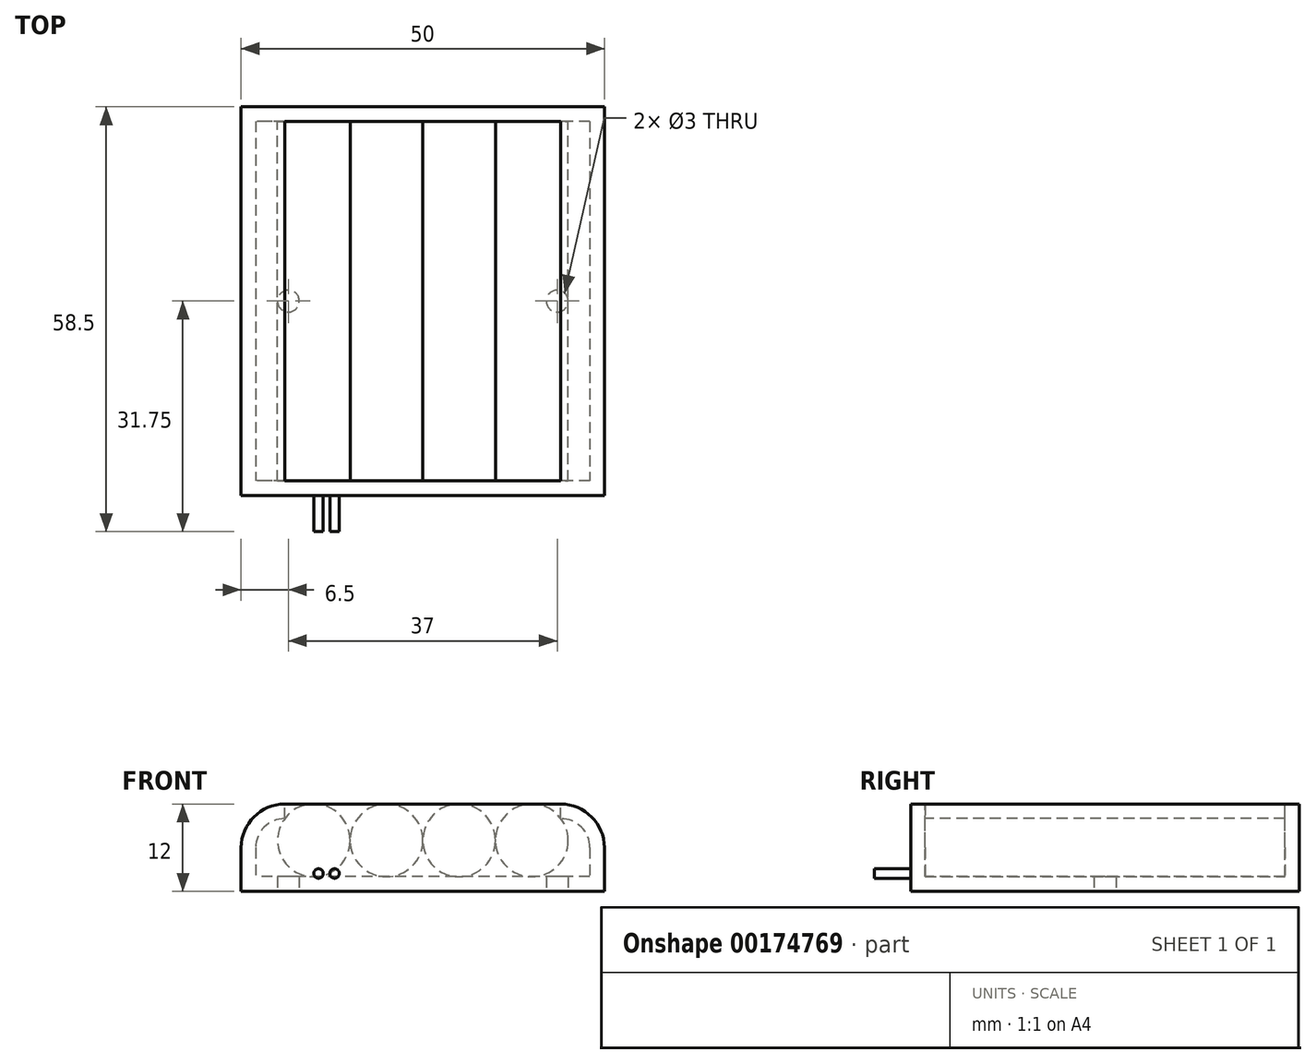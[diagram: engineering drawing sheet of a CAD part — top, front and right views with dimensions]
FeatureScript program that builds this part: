
annotation { "Feature Type Name" : "Feature", "Feature Type Description" : "" }
export const myFeature = defineFeature(function(context is Context, id is Id, definition is map)
    precondition{}
    {
        {
            var Q0;
            Q0=qCreatedBy(makeId("Top.planeOp"),FACE);
            var sketch = newSketch(context, id + "F0", { "sketchPlane" : qUnion([Q0])});
            skLineSegment(sketch, "E0.bottom", {"start": v(25, 26.75) * mm, "end": v(-25, 26.75) * mm});
            skLineSegment(sketch, "E0.top", {"start": v(25, -26.75) * mm, "end": v(-25, -26.75) * mm});
            skLineSegment(sketch, "E0.left", {"start": v(25, 26.75) * mm, "end": v(25, -26.75) * mm});
            skLineSegment(sketch, "E0.right", {"start": v(-25, 26.75) * mm, "end": v(-25, -26.75) * mm});
            skPoint(sketch, "E0.middle", {"position": v(0, 0) * mm});
            skSolve(sketch);
        }
        {
            var Q0;
            Q0=qSketchRegion(id+"F0",true);
            extrude(context, id + "F1", {"entities" : qUnion([Q0]), "depth" : 12 * mm, "offsetDistance" : 25 * mm});
        }
        {
            var Q0;
            Q0=makeQuery(id+"F1.opExtrude","CAP_EDGE",EDGE,{"disambiguationData":[OSD([sQuery(id+"F0.wireOp",EDGE,"E0.left")])],"isStart":false});
            var Q1;
            Q1=makeQuery(id+"F1.opExtrude","CAP_EDGE",EDGE,{"disambiguationData":[OSD([sQuery(id+"F0.wireOp",EDGE,"E0.right")])],"isStart":false});
            fillet(context, id + "F2", {"entities" : qUnion([Q0, Q1]), "radius" : 6 * mm, "tangentPropagation" : true, "allowEdgeOverflow" : false});
        }
        {
            var Q0;
            Q0=makeQuery(id+"F1.opExtrude","CAP_FACE",FACE,{"disambiguationData":[OSD([sQuery(id+"F0.wireOp",EDGE,"E0.bottom"),sQuery(id+"F0.wireOp",EDGE,"E0.top"),sQuery(id+"F0.wireOp",EDGE,"E0.left"),sQuery(id+"F0.wireOp",EDGE,"E0.right")])],"isStart":false});
            shell(context, id + "F3", {"entities" : qUnion([Q0]), "thickness" : 2 * mm});
        }
        {
            var Q0;
            Q0=makeQuery(id+"F1.opExtrude","CAP_FACE",FACE,{"disambiguationData":[OSD([sQuery(id+"F0.wireOp",EDGE,"E0.bottom"),sQuery(id+"F0.wireOp",EDGE,"E0.top"),sQuery(id+"F0.wireOp",EDGE,"E0.left"),sQuery(id+"F0.wireOp",EDGE,"E0.right")])],"isStart":true});
            var sketch = newSketch(context, id + "F4", { "sketchPlane" : qUnion([Q0])});
            skCircle(sketch, "E1", {"center": v(-18.5, 0) * mm, "radius": 1.5 * mm});
            skCircle(sketch, "E2.MirrorC", {"center": v(18.5, 0) * mm, "radius": 1.5 * mm});
            skSolve(sketch);
        }
        {
            var Q0;
            Q0=qSketchRegion(id+"F4",true);
            extrude(context, id + "F5", {"entities" : qUnion([Q0]), "operationType" : NewBodyOperationType.REMOVE, "oppositeDirection" : true, "depth" : 3 * mm, "offsetDistance" : 25 * mm});
        }
        {
            var Q0;
            Q0=makeQuery(id+"F1.opExtrude","SWEPT_FACE",FACE,{"disambiguationData":[OSD([sQuery(id+"F0.wireOp",EDGE,"E0.top")])]});
            var sketch = newSketch(context, id + "F6", { "sketchPlane" : qUnion([Q0])});
            skCircle(sketch, "E3", {"center": v(-14.35, 2.45) * mm, "radius": 0.65 * mm});
            skCircle(sketch, "E4", {"center": v(-12.15, 2.45) * mm, "radius": 0.65 * mm});
            skSolve(sketch);
        }
        {
            var Q0;
            Q0=qSketchRegion(id+"F6",true);
            extrude(context, id + "F7", {"entities" : qUnion([Q0]), "operationType" : NewBodyOperationType.ADD, "depth" : 5 * mm, "offsetDistance" : 25 * mm});
        }
        {
            var Q0;
            Q0=makeQuery(id+"F3.opShell","OFFSET_FACE",FACE,{"disambiguationData":[OSD([sQuery(id+"F0.wireOp",EDGE,"E0.bottom")])]});
            var sketch = newSketch(context, id + "F8", { "sketchPlane" : qUnion([Q0])});
            skCircle(sketch, "E5", {"center": v(-15, 7) * mm, "radius": 5 * mm});
            skCircle(sketch, "E6", {"center": v(-5, 7) * mm, "radius": 5 * mm});
            skCircle(sketch, "E7.MirrorC", {"center": v(15, 7) * mm, "radius": 5 * mm});
            skCircle(sketch, "E8.MirrorC", {"center": v(5, 7) * mm, "radius": 5 * mm});
            skSolve(sketch);
        }
        {
            var Q0;
            Q0 = qSketchRegion(id + "F8", true);
            extrude(context, id + "F9", {"entities" : qUnion([Q0]), "endBound" : BoundingType.UP_TO_NEXT, "depth" : 25 * mm, "offsetDistance" : 25 * mm});
        }
    });
